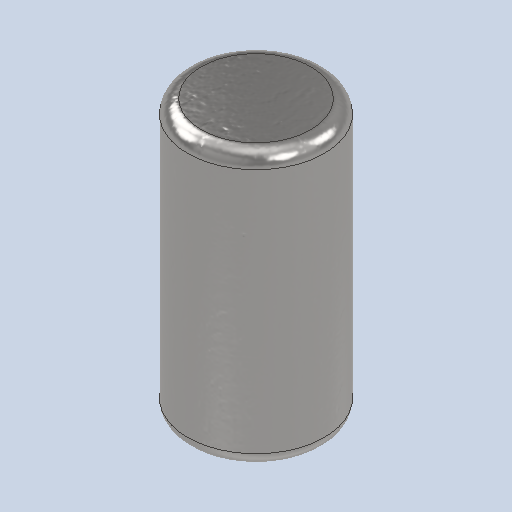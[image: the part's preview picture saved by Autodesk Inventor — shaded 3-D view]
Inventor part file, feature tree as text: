
AUTODESK INVENTOR PART (.ipt)
format: ipt  version: 2024 (Build 280153000, 153)  size: 138,752 bytes
history: native  units: in
note: dims shown in document units (in); Inventor stores cm internally (conversion verified against a paired STEP export)
features: fillet x1
ambient origin geometry x8: Origin, YZ Plane, XZ Plane, XY Plane, X Axis, Y Axis, Z Axis, Center Point
bodies: Solid1 (feature_tree)
feature tree (1):
  fillet  "Fillet1"  [1 undecoded]
note: 1 required parameter value undecoded (feature->parameter linkage not recoverable at this tier; creation-order binding heuristic only, values carry confidence <= 0.55)
